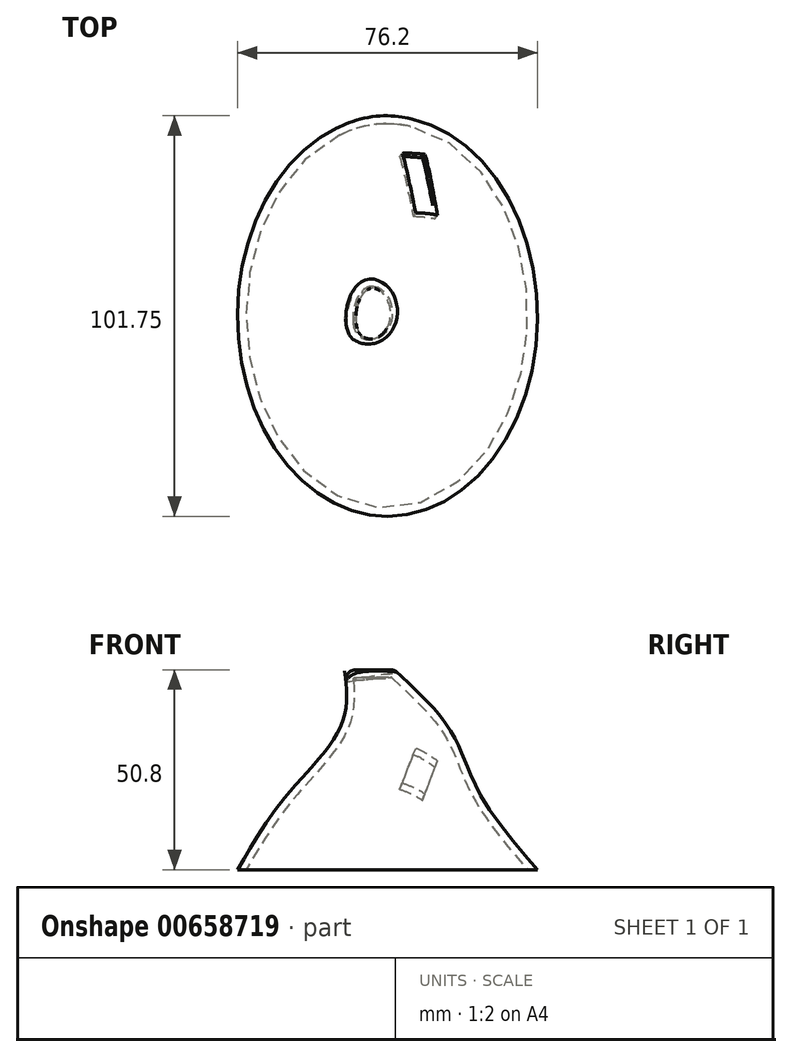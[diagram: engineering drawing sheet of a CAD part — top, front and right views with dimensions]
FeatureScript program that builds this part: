
annotation { "Feature Type Name" : "Feature", "Feature Type Description" : "" }
export const myFeature = defineFeature(function(context is Context, id is Id, definition is map)
    precondition{}
    {
        {
            var Q0;
            Q0=qCreatedBy(makeId("Top.planeOp"),FACE);
            var sketch = newSketch(context, id + "F0", { "sketchPlane" : qUnion([Q0])});
            skEllipse(sketch, "E0", {"center": v(0, 0) * mm, "majorRadius": 50.8 * mm, "minorRadius": 38.1 * mm, "majorAxis": v(0, -1)});
            skSolve(sketch);
        }
        {
            var Q0;
            Q0=qCreatedBy(makeId("Top.planeOp"),FACE);
            cPlane(context, id + "F1", {"entities" : qUnion([Q0]), "cplaneType" : CPlaneType.OFFSET, "offset" : 17.78 * mm, "width" : 152.4 * mm, "height" : 152.4 * mm});
        }
        {
            var Q0;
            Q0=qCreatedBy(id+"F1.planeOp",FACE);
            cPlane(context, id + "F2", {"entities" : qUnion([Q0]), "cplaneType" : CPlaneType.OFFSET, "offset" : 20.32 * mm, "width" : 152.4 * mm, "height" : 152.4 * mm});
        }
        {
            var Q0;
            Q0=qCreatedBy(id+"F2.planeOp",FACE);
            cPlane(context, id + "F3", {"entities" : qUnion([Q0]), "cplaneType" : CPlaneType.OFFSET, "offset" : 12.7 * mm, "width" : 152.4 * mm, "height" : 152.4 * mm});
        }
        {
            var Q0;
            Q0=qCreatedBy(id+"F1.planeOp",FACE);
            var sketch = newSketch(context, id + "F4", { "sketchPlane" : qUnion([Q0])});
            skEllipse(sketch, "E1", {"center": v(-1.1, 2.3) * mm, "majorRadius": 44.45 * mm, "minorRadius": 25.4 * mm, "majorAxis": v(0, -1)});
            skSolve(sketch);
        }
        {
            var Q0;
            Q0=qCreatedBy(id+"F2.planeOp",FACE);
            var sketch = newSketch(context, id + "F5", { "sketchPlane" : qUnion([Q0])});
            skEllipse(sketch, "E2", {"center": v(1.44, -4.76) * mm, "majorRadius": 22.23 * mm, "minorRadius": 12.7 * mm, "majorAxis": v(0, -1)});
            skSolve(sketch);
        }
        {
            var Q0;
            Q0=qCreatedBy(id+"F3.planeOp",FACE);
            var sketch = newSketch(context, id + "F6", { "sketchPlane" : qUnion([Q0])});
            skEllipse(sketch, "E3", {"center": v(-4.57, 1.19) * mm, "majorRadius": 7.62 * mm, "minorRadius": 6.35 * mm, "majorAxis": v(0, -1)});
            skSolve(sketch);
        }
        {
            var Q0;
            Q0=makeQuery(id+"F0.imprint","IMPRINT",FACE,{"disambiguationData":[TD([[makeQuery(id+"F0.imprint","IMPRINT",EDGE,{"derivedFrom":sQuery(id+"F0.wireOp",EDGE,"E0")}),1.0]])]});
            var Q1;
            Q1=makeQuery(id+"F4.imprint","IMPRINT",FACE,{"disambiguationData":[TD([[makeQuery(id+"F4.imprint","IMPRINT",EDGE,{"derivedFrom":sQuery(id+"F4.wireOp",EDGE,"E1")}),1.0]])]});
            var Q2;
            Q2=makeQuery(id+"F5.imprint","IMPRINT",FACE,{"disambiguationData":[TD([[makeQuery(id+"F5.imprint","IMPRINT",EDGE,{"derivedFrom":sQuery(id+"F5.wireOp",EDGE,"E2")}),1.0]])]});
            var Q3;
            Q3=makeQuery(id+"F6.imprint","IMPRINT",FACE,{"disambiguationData":[TD([[makeQuery(id+"F6.imprint","IMPRINT",EDGE,{"derivedFrom":sQuery(id+"F6.wireOp",EDGE,"E3")}),1.0]])]});
            loft(context, id + "F7", {"sheetProfilesArray" : [{ "sheetProfileEntities" : qUnion([Q0]) }, { "sheetProfileEntities" : qUnion([Q1]) }, { "sheetProfileEntities" : qUnion([Q2]) }, { "sheetProfileEntities" : qUnion([Q3]) }]});
        }
        {
            var Q0;
            Q0=makeQuery(id+"F7.opLoft","MID_CAP_EDGE",EDGE,{"disambiguationData":[OSD([sQuery(id+"F0.wireOp",EDGE,"E0"),sQuery(id+"F6.wireOp",EDGE,"E3")])],"capPos":3.0});
            fillet(context, id + "F8", {"entities" : qUnion([Q0]), "radius" : 2.54 * mm, "tangentPropagation" : true, "allowEdgeOverflow" : false});
        }
        {
            var Q0;
            Q0=qCreatedBy(makeId("Right.planeOp"),FACE);
            var sketch = newSketch(context, id + "F9", { "sketchPlane" : qUnion([Q0])});
            skLineSegment(sketch, "E4", {"start": v(0, 50.11) * mm, "end": v(91.06, 0) * mm});
            skSolve(sketch);
        }
        {
            var Q0;
            Q0=sQuery(id+"F9.wireOp",EDGE,"E4");
            cPlane(context, id + "F10", {"entities" : qUnion([Q0]), "cplaneType" : CPlaneType.LINE_ANGLE, "offset" : 25.4 * mm, "angle" : 20 * degree, "width" : 152.4 * mm, "height" : 152.4 * mm});
        }
        {
            var Q0;
            Q0=makeQuery(id+"F7.opLoft","CAP_FACE",FACE,{"disambiguationData":[OSD([makeQuery(id+"F0.imprint","IMPRINT",FACE,{"disambiguationData":[TD([[makeQuery(id+"F0.imprint","IMPRINT",EDGE,{"derivedFrom":sQuery(id+"F0.wireOp",EDGE,"E0")}),1.0]])]})])],"isStart":true});
            shell(context, id + "F11", {"entities" : qUnion([Q0]), "thickness" : 1.9 * mm});
        }
        {
            var Q0;
            Q0=qCreatedBy(id+"F10.planeOp",FACE);
            var sketch = newSketch(context, id + "F12", { "sketchPlane" : qUnion([Q0])});
            skLineSegment(sketch, "E5.bottom", {"start": v(-9.86, 25.67) * mm, "end": v(-3.6, 26.75) * mm});
            skLineSegment(sketch, "E5.left", {"start": v(-9.86, 25.67) * mm, "end": v(-6.83, 8.15) * mm});
            skLineSegment(sketch, "E6", {"start": v(-3.6, 26.75) * mm, "end": v(-0.57, 9.23) * mm});
            skLineSegment(sketch, "E7", {"start": v(-6.83, 8.15) * mm, "end": v(-0.57, 9.23) * mm});
            skSolve(sketch);
        }
        {
            var Q0;
            Q0=makeQuery(id+"F12.imprint","IMPRINT",FACE,{"disambiguationData":[TD([[makeQuery(id+"F12.imprint","IMPRINT",EDGE,{"derivedFrom":sQuery(id+"F12.wireOp",EDGE,"E5.bottom")}),-1.0]])]});
            extrude(context, id + "F13", {"entities" : qUnion([Q0]), "operationType" : NewBodyOperationType.REMOVE, "oppositeDirection" : true, "depth" : 12.7 * mm, "offsetDistance" : 25.4 * mm});
        }
    });
